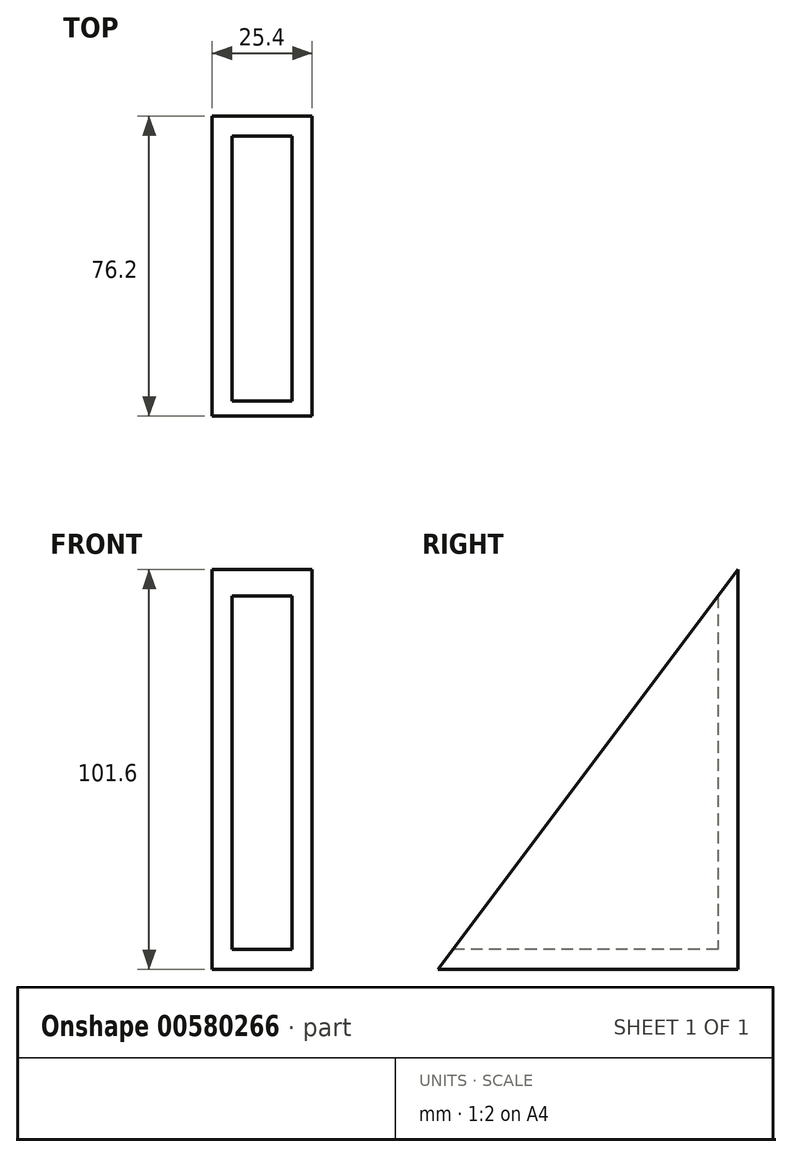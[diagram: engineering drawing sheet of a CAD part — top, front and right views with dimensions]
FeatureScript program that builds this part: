
annotation { "Feature Type Name" : "Feature", "Feature Type Description" : "" }
export const myFeature = defineFeature(function(context is Context, id is Id, definition is map)
    precondition{}
    {
        {
            var Q0;
            Q0=qCreatedBy(makeId("Right.planeOp"),FACE);
            var sketch = newSketch(context, id + "F0", { "sketchPlane" : qUnion([Q0])});
            skLineSegment(sketch, "E0", {"start": v(0, -25.7) * mm, "end": v(-76.2, -25.7) * mm});
            skLineSegment(sketch, "E1", {"start": v(-76.2, -25.7) * mm, "end": v(0, 75.9) * mm});
            skLineSegment(sketch, "E2", {"start": v(0, 75.9) * mm, "end": v(0, -25.7) * mm});
            skSolve(sketch);
        }
        {
            var Q0;
            Q0 = qSketchRegion(id + "F0", true);
            extrude(context, id + "F1", {"entities" : qUnion([Q0]), "depth" : 25.4 * mm, "offsetDistance" : 25.4 * mm});
        }
        {
            var Q0;
            Q0=makeQuery(id+"F1.opExtrude","SWEPT_FACE",FACE,{"disambiguationData":[OSD([sQuery(id+"F0.wireOp",EDGE,"E1")])]});
            shell(context, id + "F2", {"entities" : qUnion([Q0]), "thickness" : 5.08 * mm});
        }
    });
